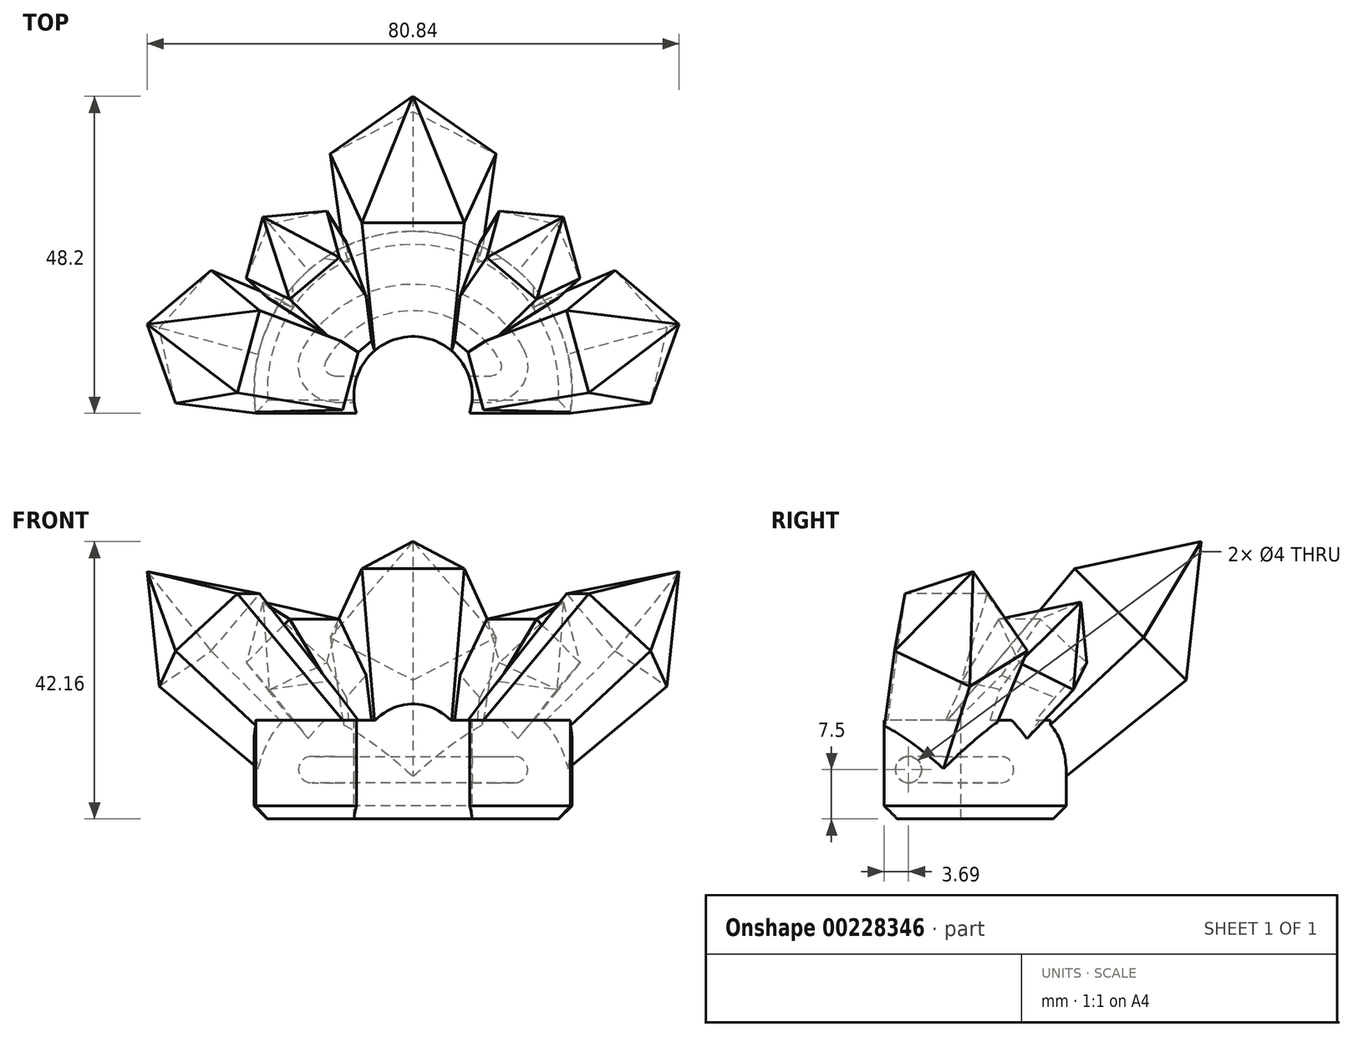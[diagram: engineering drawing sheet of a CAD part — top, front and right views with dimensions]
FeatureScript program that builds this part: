
annotation { "Feature Type Name" : "Feature", "Feature Type Description" : "" }
export const myFeature = defineFeature(function(context is Context, id is Id, definition is map)
    precondition{}
    {
        {
            var Q0;
            Q0=qCreatedBy(makeId("Top.planeOp"),FACE);
            var sketch = newSketch(context, id + "F0", { "sketchPlane" : qUnion([Q0])});
            skLineSegment(sketch, "E0", {"start": v(0, 0) * mm, "end": v(17, 0) * mm, "construction": true});
            skLineSegment(sketch, "E1", {"start": v(0, 0) * mm, "end": v(-17, 0) * mm, "construction": true});
            skArc(sketch, "E2", {"start": v(17, 0) * mm, "mid": v(0, 15) * mm, "end": v(-17, 0) * mm, "construction": true});
            skCircle(sketch, "E3.cCircle", {"center": v(0, 15) * mm, "radius": 8.1 * mm, "construction": true});
            skLineSegment(sketch, "E3.0", {"start": v(0, 25) * mm, "end": v(9.51, 18.1) * mm});
            skLineSegment(sketch, "E3.1", {"start": v(9.51, 18.1) * mm, "end": v(5.88, 6.9) * mm});
            skLineSegment(sketch, "E3.2", {"start": v(5.88, 6.9) * mm, "end": v(-5.88, 6.9) * mm});
            skLineSegment(sketch, "E3.3", {"start": v(-5.88, 6.9) * mm, "end": v(-9.51, 18.1) * mm});
            skLineSegment(sketch, "E3.4", {"start": v(-9.51, 18.1) * mm, "end": v(0, 25) * mm});
            skPoint(sketch, "E3.0.midPoint", {"position": v(4.76, 21.55) * mm});
            skLineSegment(sketch, "E4", {"start": v(0, 0) * mm, "end": v(-18.62, 22.2) * mm, "construction": true});
            skLineSegment(sketch, "E5", {"start": v(0, 0) * mm, "end": v(20.56, 24.5) * mm, "construction": true});
            skCircle(sketch, "E6.cCircle", {"center": v(-9.93, 11.83) * mm, "radius": 5.03 * mm, "construction": true});
            skLineSegment(sketch, "E6.0", {"start": v(-13.93, 16.6) * mm, "end": v(-6.63, 17.1) * mm});
            skLineSegment(sketch, "E6.1", {"start": v(-6.63, 17.1) * mm, "end": v(-3.89, 10.33) * mm});
            skLineSegment(sketch, "E6.2", {"start": v(-3.89, 10.33) * mm, "end": v(-9.5, 5.62) * mm});
            skLineSegment(sketch, "E6.3", {"start": v(-9.5, 5.62) * mm, "end": v(-15.7, 9.5) * mm});
            skLineSegment(sketch, "E6.4", {"start": v(-15.7, 9.5) * mm, "end": v(-13.93, 16.6) * mm});
            skPoint(sketch, "E6.0.midPoint", {"position": v(-10.28, 16.85) * mm});
            skCircle(sketch, "E7.cCircle", {"center": v(9.93, 11.83) * mm, "radius": 5.03 * mm, "construction": true});
            skPoint(sketch, "E7.cCircle.perimeterSnap0", {"position": v(10.28, 12.25) * mm});
            skLineSegment(sketch, "E7.0", {"start": v(6.63, 17.1) * mm, "end": v(13.93, 16.6) * mm});
            skLineSegment(sketch, "E7.1", {"start": v(13.93, 16.6) * mm, "end": v(15.7, 9.5) * mm});
            skLineSegment(sketch, "E7.2", {"start": v(15.7, 9.5) * mm, "end": v(9.5, 5.62) * mm});
            skLineSegment(sketch, "E7.3", {"start": v(9.5, 5.62) * mm, "end": v(3.89, 10.33) * mm});
            skLineSegment(sketch, "E7.4", {"start": v(3.89, 10.33) * mm, "end": v(6.63, 17.1) * mm});
            skPoint(sketch, "E7.0.midPoint", {"position": v(10.28, 16.85) * mm});
            skPoint(sketch, "E7.0.midPoint.positionSnap0", {"position": v(10.28, 12.25) * mm});
            skLineSegment(sketch, "E8", {"start": v(0, 0) * mm, "end": v(0, 46.04) * mm, "construction": true});
            skLineSegment(sketch, "E9", {"start": v(0, 0) * mm, "end": v(-35.68, 9.56) * mm, "construction": true});
            skLineSegment(sketch, "E10", {"start": v(0, 0) * mm, "end": v(44.39, 11.9) * mm, "construction": true});
            skPoint(sketch, "E11", {"position": v(-15.9, 4.26) * mm});
            skPoint(sketch, "E12", {"position": v(15.9, 4.26) * mm});
            skCircle(sketch, "E13.cCircle", {"center": v(-15.9, 4.26) * mm, "radius": 6.7 * mm, "construction": true});
            skLineSegment(sketch, "E13.0", {"start": v(-23.9, 6.4) * mm, "end": v(-16.33, 12.53) * mm});
            skLineSegment(sketch, "E13.1", {"start": v(-16.33, 12.53) * mm, "end": v(-8.16, 7.23) * mm});
            skLineSegment(sketch, "E13.2", {"start": v(-8.16, 7.23) * mm, "end": v(-10.68, -2.18) * mm});
            skLineSegment(sketch, "E13.3", {"start": v(-10.68, -2.18) * mm, "end": v(-20.4, -2.69) * mm});
            skLineSegment(sketch, "E13.4", {"start": v(-20.4, -2.69) * mm, "end": v(-23.9, 6.4) * mm});
            skPoint(sketch, "E13.0.midPoint", {"position": v(-20.11, 9.47) * mm});
            skCircle(sketch, "E14.cCircle", {"center": v(15.9, 4.26) * mm, "radius": 6.7 * mm, "construction": true});
            skLineSegment(sketch, "E14.0", {"start": v(16.33, 12.53) * mm, "end": v(23.9, 6.4) * mm});
            skLineSegment(sketch, "E14.1", {"start": v(23.9, 6.4) * mm, "end": v(20.4, -2.69) * mm});
            skLineSegment(sketch, "E14.2", {"start": v(20.4, -2.69) * mm, "end": v(10.68, -2.18) * mm});
            skLineSegment(sketch, "E14.3", {"start": v(10.68, -2.18) * mm, "end": v(8.16, 7.23) * mm});
            skLineSegment(sketch, "E14.4", {"start": v(8.16, 7.23) * mm, "end": v(16.33, 12.53) * mm});
            skPoint(sketch, "E14.0.midPoint", {"position": v(20.11, 9.47) * mm});
            skLineSegment(sketch, "E15", {"start": v(-23.9, -2.69) * mm, "end": v(23.9, -2.69) * mm});
            skLineSegment(sketch, "E16", {"start": v(-23.9, 6.4) * mm, "end": v(-23.9, -12.7) * mm, "construction": true});
            skLineSegment(sketch, "E17", {"start": v(23.9, 6.4) * mm, "end": v(23.9, -14.68) * mm, "construction": true});
            skArc(sketch, "E18", {"start": v(23.9, -2.69) * mm, "mid": v(0, 25) * mm, "end": v(-23.9, -2.69) * mm});
            skLineSegment(sketch, "E19.top", {"start": v(-23.9, -5.6) * mm, "end": v(23.9, -5.6) * mm});
            skLineSegment(sketch, "E19.left", {"start": v(-23.9, -2.69) * mm, "end": v(-23.9, -5.6) * mm});
            skLineSegment(sketch, "E19.right", {"start": v(23.9, -2.69) * mm, "end": v(23.9, -5.6) * mm});
            skSolve(sketch);
        }
        {
            var Q0;
            Q0=qCreatedBy(makeId("Top.planeOp"),FACE);
            var sketch = newSketch(context, id + "F1", { "sketchPlane" : qUnion([Q0])});
            skArc(sketch, "E20.0", {"start": v(18.92, 0.72) * mm, "mid": v(0, 17) * mm, "end": v(-18.92, 0.72) * mm});
            skCircle(sketch, "E21", {"center": v(0, 0) * mm, "radius": 9 * mm});
            skLineSegment(sketch, "E22.0", {"start": v(-17.44, -1) * mm, "end": v(0, -1) * mm});
            skLineSegment(sketch, "E23.trimOffspring", {"start": v(-14.93, 1) * mm, "end": v(14.93, 1) * mm, "construction": true});
            skLineSegment(sketch, "E24.trimOffspring", {"start": v(-11.91, 3) * mm, "end": v(0, 3) * mm});
            skArc(sketch, "E25.trimOffspring", {"start": v(13.22, 5.23) * mm, "mid": v(0, 13) * mm, "end": v(-13.22, 5.23) * mm});
            skArc(sketch, "E26.trimOffspring", {"start": v(16.36, 2.94) * mm, "mid": v(0, 15) * mm, "end": v(-16.36, 2.94) * mm, "construction": true});
            skLineSegment(sketch, "E27", {"start": v(0, 3) * mm, "end": v(0, 1) * mm});
            skLineSegment(sketch, "E28", {"start": v(0, 3) * mm, "end": v(11.91, 3) * mm});
            skLineSegment(sketch, "E29", {"start": v(0, 1) * mm, "end": v(0, -1) * mm});
            skLineSegment(sketch, "E30", {"start": v(0, -1) * mm, "end": v(17.44, -1) * mm});
            skPoint(sketch, "E31.visualSharp", {"position": v(19.1, -1) * mm});
            skArc(sketch, "E31.filletArc", {"start": v(17.44, -1) * mm, "mid": v(18.57, -0.48) * mm, "end": v(18.92, 0.72) * mm});
            skPoint(sketch, "E32.visualSharp", {"position": v(-19.1, -1) * mm});
            skArc(sketch, "E32.filletArc", {"start": v(-18.92, 0.72) * mm, "mid": v(-18.57, -0.48) * mm, "end": v(-17.44, -1) * mm});
            skPoint(sketch, "E33.newPointB", {"position": v(-18.43, 3) * mm});
            skArc(sketch, "E33.filletArc", {"start": v(-13.22, 5.23) * mm, "mid": v(-13.2, 3.74) * mm, "end": v(-11.91, 3) * mm});
            skArc(sketch, "E34.filletArc", {"start": v(11.91, 3) * mm, "mid": v(13.2, 3.74) * mm, "end": v(13.22, 5.23) * mm});
            skPoint(sketch, "E35.visualSharp", {"position": v(16.84, 1) * mm});
            skArc(sketch, "E35.filletArc", {"start": v(14.93, 1) * mm, "mid": v(16.14, 1.61) * mm, "end": v(16.36, 2.94) * mm, "construction": true});
            skPoint(sketch, "E36.visualSharp", {"position": v(-16.84, 1) * mm});
            skArc(sketch, "E36.filletArc", {"start": v(-16.36, 2.94) * mm, "mid": v(-16.14, 1.61) * mm, "end": v(-14.93, 1) * mm, "construction": true});
            skSolve(sketch);
        }
        {
            var Q0;
            Q0=qCreatedBy(makeId("Front.planeOp"),FACE);
            var sketch = newSketch(context, id + "F2", { "sketchPlane" : qUnion([Q0])});
            skCircle(sketch, "E37", {"center": v(-17, -7.5) * mm, "radius": 2 * mm});
            skCircle(sketch, "E38", {"center": v(17, -7.5) * mm, "radius": 2 * mm});
            skSolve(sketch);
        }
        {
            var Q0;
            {var subQ0=sQuery(id+"F0.wireOp",EDGE,"E13.0");Q0=makeQuery(id+"F0.imprint","IMPRINT",FACE,{"disambiguationData":[TD([[makeQuery(id+"F0.imprint","IMPRINT",EDGE,{"derivedFrom":subQ0}),-1.0]])]});}
            var Q1;
            {var subQ0=sQuery(id+"F0.wireOp",EDGE,"E13.1");var subQ1=sQuery(id+"F0.wireOp",EDGE,"E2");var subQ2=makeQuery(id+"F0.imprint","INTERSECT",VERTEX,{"derivedFrom":[subQ1,subQ0]});Q1=makeQuery(id+"F0.imprint","IMPRINT",FACE,{"disambiguationData":[TD([[makeQuery(id+"F0.imprint","IMPRINT",EDGE,{"disambiguationData":[TD([[subQ2,-1.0]])],"derivedFrom":subQ1}),-1.0]])]});}
            var Q2;
            {var subQ0=sQuery(id+"F0.wireOp",EDGE,"E13.1");var subQ1=sQuery(id+"F0.wireOp",EDGE,"E2");var subQ2=makeQuery(id+"F0.imprint","INTERSECT",VERTEX,{"derivedFrom":[subQ1,subQ0]});Q2=makeQuery(id+"F0.imprint","IMPRINT",FACE,{"disambiguationData":[TD([[makeQuery(id+"F0.imprint","IMPRINT",EDGE,{"disambiguationData":[TD([[subQ2,-1.0]])],"derivedFrom":subQ1}),1.0]])]});}
            var Q3;
            {var subQ0=sQuery(id+"F0.wireOp",EDGE,"E6.3");var subQ6=sQuery(id+"F0.wireOp",EDGE,"E2");var subQ10=makeQuery(id+"F0.imprint","INTERSECT",VERTEX,{"derivedFrom":[subQ6,subQ0]});Q3=makeQuery(id+"F0.imprint","IMPRINT",FACE,{"disambiguationData":[TD([[makeQuery(id+"F0.imprint","IMPRINT",EDGE,{"disambiguationData":[TD([[subQ10,-1.0]])],"derivedFrom":subQ6}),1.0]])]});}
            var Q4;
            {var subQ0=sQuery(id+"F0.wireOp",EDGE,"E2");var subQ1=sQuery(id+"F0.wireOp",EDGE,"E1");var subQ2=makeQuery(id+"F0.imprint","INTERSECT",VERTEX,{"derivedFrom":[subQ1,subQ0]});Q4=makeQuery(id+"F0.imprint","IMPRINT",FACE,{"disambiguationData":[TD([[makeQuery(id+"F0.imprint","IMPRINT",EDGE,{"disambiguationData":[TD([[subQ2,1.0]])],"derivedFrom":subQ1}),-1.0]])]});}
            var Q5;
            {var subQ4=sQuery(id+"F0.wireOp",EDGE,"E13.3");Q5=makeQuery(id+"F0.imprint","IMPRINT",FACE,{"disambiguationData":[TD([[makeQuery(id+"F0.imprint","IMPRINT",EDGE,{"derivedFrom":subQ4}),-1.0]])]});}
            var Q6;
            {var subQ0=sQuery(id+"F0.wireOp",EDGE,"E7.2");var subQ1=sQuery(id+"F0.wireOp",EDGE,"E2");var subQ2=makeQuery(id+"F0.imprint","INTERSECT",VERTEX,{"derivedFrom":[subQ1,subQ0]});Q6=makeQuery(id+"F0.imprint","IMPRINT",FACE,{"disambiguationData":[TD([[makeQuery(id+"F0.imprint","IMPRINT",EDGE,{"disambiguationData":[TD([[subQ2,-1.0]])],"derivedFrom":subQ1}),1.0]])]});}
            var Q7;
            {var subQ0=sQuery(id+"F0.wireOp",EDGE,"E7.2");var subQ1=sQuery(id+"F0.wireOp",EDGE,"E2");var subQ2=makeQuery(id+"F0.imprint","INTERSECT",VERTEX,{"derivedFrom":[subQ1,subQ0]});Q7=makeQuery(id+"F0.imprint","IMPRINT",FACE,{"disambiguationData":[TD([[makeQuery(id+"F0.imprint","IMPRINT",EDGE,{"disambiguationData":[TD([[subQ2,-1.0]])],"derivedFrom":subQ1}),-1.0]])]});}
            var Q8;
            {var subQ0=sQuery(id+"F0.wireOp",EDGE,"E14.0");Q8=makeQuery(id+"F0.imprint","IMPRINT",FACE,{"disambiguationData":[TD([[makeQuery(id+"F0.imprint","IMPRINT",EDGE,{"derivedFrom":subQ0}),-1.0]])]});}
            var Q9;
            {var subQ0=sQuery(id+"F0.wireOp",EDGE,"E14.1");Q9=makeQuery(id+"F0.imprint","IMPRINT",FACE,{"disambiguationData":[TD([[makeQuery(id+"F0.imprint","IMPRINT",EDGE,{"derivedFrom":subQ0}),-1.0]])]});}
            var Q10;
            {var subQ7=sQuery(id+"F0.wireOp",EDGE,"E10");var subQ9=sQuery(id+"F0.wireOp",EDGE,"E2");var subQ11=makeQuery(id+"F0.imprint","INTERSECT",VERTEX,{"derivedFrom":[subQ9,subQ7]});Q10=makeQuery(id+"F0.imprint","IMPRINT",FACE,{"disambiguationData":[TD([[makeQuery(id+"F0.imprint","IMPRINT",EDGE,{"disambiguationData":[TD([[subQ11,-1.0]])],"derivedFrom":subQ9}),1.0]])]});}
            var Q11;
            {var subQ0=sQuery(id+"F0.wireOp",EDGE,"E2");var subQ1=sQuery(id+"F0.wireOp",EDGE,"E0");var subQ2=makeQuery(id+"F0.imprint","INTERSECT",VERTEX,{"derivedFrom":[subQ1,subQ0]});Q11=makeQuery(id+"F0.imprint","IMPRINT",FACE,{"disambiguationData":[TD([[makeQuery(id+"F0.imprint","IMPRINT",EDGE,{"disambiguationData":[TD([[subQ2,1.0]])],"derivedFrom":subQ1}),1.0]])]});}
            var Q12;
            {var subQ0=sQuery(id+"F0.wireOp",EDGE,"E14.2");Q12=makeQuery(id+"F0.imprint","IMPRINT",FACE,{"disambiguationData":[TD([[makeQuery(id+"F0.imprint","IMPRINT",EDGE,{"derivedFrom":subQ0}),-1.0]])]});}
            var Q13;
            {var subQ0=sQuery(id+"F0.wireOp",EDGE,"E10");var subQ1=sQuery(id+"F0.wireOp",EDGE,"E2");var subQ2=makeQuery(id+"F0.imprint","INTERSECT",VERTEX,{"derivedFrom":[subQ1,subQ0]});Q13=makeQuery(id+"F0.imprint","IMPRINT",FACE,{"disambiguationData":[TD([[makeQuery(id+"F0.imprint","IMPRINT",EDGE,{"disambiguationData":[TD([[subQ2,-1.0]])],"derivedFrom":subQ1}),-1.0]])]});}
            var Q14;
            {var subQ1=sQuery(id+"F0.wireOp",EDGE,"E2");var subQ10=sQuery(id+"F0.wireOp",EDGE,"E6.3");var subQ13=makeQuery(id+"F0.imprint","INTERSECT",VERTEX,{"derivedFrom":[subQ1,subQ10]});Q14=makeQuery(id+"F0.imprint","IMPRINT",FACE,{"disambiguationData":[TD([[makeQuery(id+"F0.imprint","IMPRINT",EDGE,{"disambiguationData":[TD([[subQ13,-1.0]])],"derivedFrom":subQ1}),-1.0]])]});}
            var Q15;
            {var subQ0=sQuery(id+"F0.wireOp",EDGE,"E13.4");Q15=makeQuery(id+"F0.imprint","IMPRINT",FACE,{"disambiguationData":[TD([[makeQuery(id+"F0.imprint","IMPRINT",EDGE,{"derivedFrom":subQ0}),-1.0]])]});}
            var Q16;
            {var subQ0=sQuery(id+"F0.wireOp",EDGE,"E6.3");Q16=makeQuery(id+"F0.imprint","IMPRINT",FACE,{"disambiguationData":[TD([[makeQuery(id+"F0.imprint","IMPRINT",EDGE,{"derivedFrom":subQ0}),-1.0]])]});}
            var Q17;
            {var subQ0=sQuery(id+"F0.wireOp",EDGE,"E7.2");Q17=makeQuery(id+"F0.imprint","IMPRINT",FACE,{"disambiguationData":[TD([[makeQuery(id+"F0.imprint","IMPRINT",EDGE,{"derivedFrom":subQ0}),-1.0]])]});}
            extrude(context, id + "F3", {"entities" : qUnion([Q0, Q1, Q2, Q3, Q4, Q5, Q6, Q7, Q8, Q9, Q10, Q11, Q12, Q13, Q14, Q15, Q16, Q17]), "depth" : 25 * mm, "hasDraft" : true, "draftAngle" : 5 * degree});
        }
        {
            var Q0;
            Q0=makeQuery(id+"F3.opExtrude","SWEPT_BODY",BODY,{"disambiguationData":[OSD([sQuery(id+"F0.wireOp",EDGE,"E13.0"),sQuery(id+"F0.wireOp",EDGE,"E13.1"),sQuery(id+"F0.wireOp",EDGE,"E13.2"),sQuery(id+"F0.wireOp",EDGE,"E13.3"),sQuery(id+"F0.wireOp",EDGE,"E13.4")])]});
            var Q1;
            Q1=sQuery(id+"F0.wireOp",EDGE,"E13.2");
            transform(context, id + "F4", {"entities" : qUnion([Q0]), "transformType" : TransformType.ROTATION, "transformAxis" : qUnion([Q1]), "angle" : 45 * degree, "makeCopy" : false});
        }
        {
            var Q0;
            Q0=makeQuery(id+"F3.opExtrude","CAP_FACE",FACE,{"disambiguationData":[OSD([sQuery(id+"F0.wireOp",EDGE,"E13.0"),sQuery(id+"F0.wireOp",EDGE,"E13.1"),sQuery(id+"F0.wireOp",EDGE,"E13.2"),sQuery(id+"F0.wireOp",EDGE,"E13.3"),sQuery(id+"F0.wireOp",EDGE,"E13.4")])],"isStart":false});
            extrude(context, id + "F5", {"entities" : qUnion([Q0]), "operationType" : NewBodyOperationType.ADD, "depth" : 16 * mm, "hasDraft" : true, "draftAngle" : 33 * degree, "draftPullDirection" : true});
        }
        {
            var Q0;
            Q0=makeQuery(id+"F3.opExtrude","SWEPT_BODY",BODY,{"disambiguationData":[OSD([sQuery(id+"F0.wireOp",EDGE,"E14.0"),sQuery(id+"F0.wireOp",EDGE,"E14.1"),sQuery(id+"F0.wireOp",EDGE,"E14.2"),sQuery(id+"F0.wireOp",EDGE,"E14.3"),sQuery(id+"F0.wireOp",EDGE,"E14.4")])]});
            var Q1;
            Q1=sQuery(id+"F0.wireOp",EDGE,"E14.3");
            transform(context, id + "F6", {"entities" : qUnion([Q0]), "transformType" : TransformType.ROTATION, "transformAxis" : qUnion([Q1]), "angle" : 45 * degree, "makeCopy" : false});
        }
        {
            var Q0;
            Q0=makeQuery(id+"F3.opExtrude","CAP_FACE",FACE,{"disambiguationData":[OSD([sQuery(id+"F0.wireOp",EDGE,"E14.0"),sQuery(id+"F0.wireOp",EDGE,"E14.1"),sQuery(id+"F0.wireOp",EDGE,"E14.2"),sQuery(id+"F0.wireOp",EDGE,"E14.3"),sQuery(id+"F0.wireOp",EDGE,"E14.4")])],"isStart":false});
            extrude(context, id + "F7", {"entities" : qUnion([Q0]), "operationType" : NewBodyOperationType.ADD, "depth" : 19 * mm, "hasDraft" : true, "draftAngle" : 33 * degree, "draftPullDirection" : true});
        }
        {
            var Q0;
            {var subQ1=sQuery(id+"F0.wireOp",EDGE,"E3.2");Q0=makeQuery(id+"F0.imprint","IMPRINT",FACE,{"disambiguationData":[TD([[makeQuery(id+"F0.imprint","IMPRINT",EDGE,{"derivedFrom":subQ1}),-1.0]])]});}
            var Q1;
            {var subQ0=sQuery(id+"F0.wireOp",EDGE,"E3.1");var subQ1=sQuery(id+"F0.wireOp",EDGE,"E2");var subQ2=makeQuery(id+"F0.imprint","INTERSECT",VERTEX,{"derivedFrom":[subQ1,subQ0]});Q1=makeQuery(id+"F0.imprint","IMPRINT",FACE,{"disambiguationData":[TD([[makeQuery(id+"F0.imprint","IMPRINT",EDGE,{"disambiguationData":[TD([[subQ2,-1.0]])],"derivedFrom":subQ1}),1.0]])]});}
            var Q2;
            {var subQ1=sQuery(id+"F0.wireOp",EDGE,"E3.0");Q2=makeQuery(id+"F0.imprint","IMPRINT",FACE,{"disambiguationData":[TD([[makeQuery(id+"F0.imprint","IMPRINT",EDGE,{"derivedFrom":subQ1}),-1.0]])]});}
            var Q3;
            {var subQ0=sQuery(id+"F0.wireOp",EDGE,"E3.1");var subQ1=sQuery(id+"F0.wireOp",EDGE,"E2");var subQ2=makeQuery(id+"F0.imprint","INTERSECT",VERTEX,{"derivedFrom":[subQ1,subQ0]});Q3=makeQuery(id+"F0.imprint","IMPRINT",FACE,{"disambiguationData":[TD([[makeQuery(id+"F0.imprint","IMPRINT",EDGE,{"disambiguationData":[TD([[subQ2,-1.0]])],"derivedFrom":subQ1}),-1.0]])]});}
            var Q4;
            {var subQ0=sQuery(id+"F0.wireOp",EDGE,"E6.1");var subQ1=sQuery(id+"F0.wireOp",EDGE,"E2");var subQ2=makeQuery(id+"F0.imprint","INTERSECT",VERTEX,{"derivedFrom":[subQ1,subQ0]});Q4=makeQuery(id+"F0.imprint","IMPRINT",FACE,{"disambiguationData":[TD([[makeQuery(id+"F0.imprint","IMPRINT",EDGE,{"disambiguationData":[TD([[subQ2,-1.0]])],"derivedFrom":subQ1}),1.0]])]});}
            var Q5;
            {var subQ0=sQuery(id+"F0.wireOp",EDGE,"E6.1");var subQ1=sQuery(id+"F0.wireOp",EDGE,"E2");var subQ2=makeQuery(id+"F0.imprint","INTERSECT",VERTEX,{"derivedFrom":[subQ1,subQ0]});Q5=makeQuery(id+"F0.imprint","IMPRINT",FACE,{"disambiguationData":[TD([[makeQuery(id+"F0.imprint","IMPRINT",EDGE,{"disambiguationData":[TD([[subQ2,-1.0]])],"derivedFrom":subQ1}),-1.0]])]});}
            var Q6;
            {var subQ5=sQuery(id+"F0.wireOp",EDGE,"E6.1");Q6=makeQuery(id+"F0.imprint","IMPRINT",FACE,{"disambiguationData":[TD([[makeQuery(id+"F0.imprint","IMPRINT",EDGE,{"derivedFrom":subQ5}),-1.0]])]});}
            var Q7;
            {var subQ5=sQuery(id+"F0.wireOp",EDGE,"E7.4");Q7=makeQuery(id+"F0.imprint","IMPRINT",FACE,{"disambiguationData":[TD([[makeQuery(id+"F0.imprint","IMPRINT",EDGE,{"derivedFrom":subQ5}),-1.0]])]});}
            extrude(context, id + "F8", {"entities" : qUnion([Q0, Q1, Q2, Q3, Q4, Q5, Q6, Q7]), "depth" : 30 * mm, "hasDraft" : true, "draftAngle" : 5 * degree});
        }
        {
            var Q0;
            Q0=makeQuery(id+"F8.opExtrude","CAP_EDGE",EDGE,{"disambiguationData":[OSD([sQuery(id+"F0.wireOp",EDGE,"E3.2")])],"isStart":true});
            cPoint(context, id + "F9", {"entities" : qUnion([Q0]), "parameter" : 0.5});
        }
        {
            var Q0;
            Q0=makeQuery(id+"F8.opExtrude","SWEPT_BODY",BODY,{"disambiguationData":[OSD([sQuery(id+"F0.wireOp",EDGE,"E3.0"),sQuery(id+"F0.wireOp",EDGE,"E3.1"),sQuery(id+"F0.wireOp",EDGE,"E3.2"),sQuery(id+"F0.wireOp",EDGE,"E3.3"),sQuery(id+"F0.wireOp",EDGE,"E3.4")])]});
            var Q1;
            Q1 = qCreatedBy(id + "F9" ,VERTEX);
            var Q2;
            Q2=makeQuery(id+"F8.opExtrude","CAP_EDGE",EDGE,{"disambiguationData":[OSD([sQuery(id+"F0.wireOp",EDGE,"E3.2")])],"isStart":true});
            transform(context, id + "F10", {"entities" : qUnion([Q0]), "transformType" : TransformType.ROTATION, "transformAxis" : qUnion([Q2]), "angle" : 45 * degree, "makeCopy" : false});
        }
        {
            var Q0;
            Q0=makeQuery(id+"F8.opExtrude","CAP_FACE",FACE,{"disambiguationData":[OSD([sQuery(id+"F0.wireOp",EDGE,"E3.0"),sQuery(id+"F0.wireOp",EDGE,"E3.1"),sQuery(id+"F0.wireOp",EDGE,"E3.2"),sQuery(id+"F0.wireOp",EDGE,"E3.3"),sQuery(id+"F0.wireOp",EDGE,"E3.4")])],"isStart":false});
            extrude(context, id + "F11", {"entities" : qUnion([Q0]), "operationType" : NewBodyOperationType.ADD, "depth" : 18 * mm, "hasDraft" : true, "draftAngle" : 33 * degree, "draftPullDirection" : true});
        }
        {
            var Q0;
            {var subQ1=sQuery(id+"F0.wireOp",EDGE,"E3.1");var subQ6=sQuery(id+"F0.wireOp",EDGE,"E7.0");var subQ9=makeQuery(id+"F0.imprint","INTERSECT",VERTEX,{"derivedFrom":[subQ1,subQ6]});Q0=makeQuery(id+"F0.imprint","IMPRINT",FACE,{"disambiguationData":[TD([[makeQuery(id+"F0.imprint","IMPRINT",EDGE,{"disambiguationData":[TD([[subQ9,-1.0]])],"derivedFrom":subQ1}),1.0]])]});}
            var Q1;
            {var subQ0=sQuery(id+"F0.wireOp",EDGE,"E7.2");Q1=makeQuery(id+"F0.imprint","IMPRINT",FACE,{"disambiguationData":[TD([[makeQuery(id+"F0.imprint","IMPRINT",EDGE,{"derivedFrom":subQ0}),-1.0]])]});}
            var Q2;
            {var subQ5=sQuery(id+"F0.wireOp",EDGE,"E7.4");Q2=makeQuery(id+"F0.imprint","IMPRINT",FACE,{"disambiguationData":[TD([[makeQuery(id+"F0.imprint","IMPRINT",EDGE,{"derivedFrom":subQ5}),-1.0]])]});}
            var Q3;
            {var subQ5=sQuery(id+"F0.wireOp",EDGE,"E6.1");Q3=makeQuery(id+"F0.imprint","IMPRINT",FACE,{"disambiguationData":[TD([[makeQuery(id+"F0.imprint","IMPRINT",EDGE,{"derivedFrom":subQ5}),-1.0]])]});}
            var Q4;
            {var subQ5=sQuery(id+"F0.wireOp",EDGE,"E6.2");var subQ6=sQuery(id+"F0.wireOp",EDGE,"E3.3");var subQ7=makeQuery(id+"F0.imprint","INTERSECT",VERTEX,{"derivedFrom":[subQ6,subQ5]});Q4=makeQuery(id+"F0.imprint","IMPRINT",FACE,{"disambiguationData":[TD([[makeQuery(id+"F0.imprint","IMPRINT",EDGE,{"disambiguationData":[TD([[subQ7,-1.0]])],"derivedFrom":subQ6}),1.0]])]});}
            var Q5;
            {var subQ0=sQuery(id+"F0.wireOp",EDGE,"E6.3");Q5=makeQuery(id+"F0.imprint","IMPRINT",FACE,{"disambiguationData":[TD([[makeQuery(id+"F0.imprint","IMPRINT",EDGE,{"derivedFrom":subQ0}),-1.0]])]});}
            extrude(context, id + "F12", {"entities" : qUnion([Q0, Q1, Q2, Q3, Q4, Q5]), "depth" : 20 * mm, "hasDraft" : true, "draftAngle" : 5 * degree});
        }
        {
            var Q0;
            Q0=makeQuery(id+"F12.opExtrude","SWEPT_BODY",BODY,{"disambiguationData":[OSD([sQuery(id+"F0.wireOp",EDGE,"E7.0"),sQuery(id+"F0.wireOp",EDGE,"E7.1"),sQuery(id+"F0.wireOp",EDGE,"E7.2"),sQuery(id+"F0.wireOp",EDGE,"E7.3"),sQuery(id+"F0.wireOp",EDGE,"E7.4")])]});
            var Q1;
            Q1=makeQuery(id+"F12.opExtrude","CAP_EDGE",EDGE,{"disambiguationData":[OSD([sQuery(id+"F0.wireOp",EDGE,"E7.3")])],"isStart":true});
            transform(context, id + "F13", {"entities" : qUnion([Q0]), "transformType" : TransformType.ROTATION, "transformAxis" : qUnion([Q1]), "angle" : 45 * degree, "makeCopy" : false});
        }
        {
            var Q0;
            Q0=makeQuery(id+"F12.opExtrude","CAP_FACE",FACE,{"disambiguationData":[OSD([sQuery(id+"F0.wireOp",EDGE,"E7.0"),sQuery(id+"F0.wireOp",EDGE,"E7.1"),sQuery(id+"F0.wireOp",EDGE,"E7.2"),sQuery(id+"F0.wireOp",EDGE,"E7.3"),sQuery(id+"F0.wireOp",EDGE,"E7.4")])],"isStart":false});
            extrude(context, id + "F14", {"entities" : qUnion([Q0]), "operationType" : NewBodyOperationType.ADD, "depth" : 12 * mm, "hasDraft" : true, "draftAngle" : 33 * degree, "draftPullDirection" : true});
        }
        {
            var Q0;
            Q0=makeQuery(id+"F12.opExtrude","SWEPT_BODY",BODY,{"disambiguationData":[OSD([sQuery(id+"F0.wireOp",EDGE,"E6.0"),sQuery(id+"F0.wireOp",EDGE,"E6.1"),sQuery(id+"F0.wireOp",EDGE,"E6.2"),sQuery(id+"F0.wireOp",EDGE,"E6.3"),sQuery(id+"F0.wireOp",EDGE,"E6.4")])]});
            var Q1;
            Q1=makeQuery(id+"F12.opExtrude","CAP_EDGE",EDGE,{"disambiguationData":[OSD([sQuery(id+"F0.wireOp",EDGE,"E6.2")])],"isStart":true});
            transform(context, id + "F15", {"entities" : qUnion([Q0]), "transformType" : TransformType.ROTATION, "transformAxis" : qUnion([Q1]), "angle" : 45 * degree, "makeCopy" : false});
        }
        {
            var Q0;
            Q0=makeQuery(id+"F12.opExtrude","CAP_FACE",FACE,{"disambiguationData":[OSD([sQuery(id+"F0.wireOp",EDGE,"E6.0"),sQuery(id+"F0.wireOp",EDGE,"E6.1"),sQuery(id+"F0.wireOp",EDGE,"E6.2"),sQuery(id+"F0.wireOp",EDGE,"E6.3"),sQuery(id+"F0.wireOp",EDGE,"E6.4")])],"isStart":false});
            extrude(context, id + "F16", {"entities" : qUnion([Q0]), "operationType" : NewBodyOperationType.ADD, "depth" : 13 * mm, "hasDraft" : true, "draftAngle" : 33 * degree, "draftPullDirection" : true});
        }
        {
            var Q0;
            {var subQ9=sQuery(id+"F0.wireOp",EDGE,"E3.4");Q0=makeQuery(id+"F0.imprint","IMPRINT",FACE,{"disambiguationData":[TD([[makeQuery(id+"F0.imprint","IMPRINT",EDGE,{"derivedFrom":subQ9}),1.0]])]});}
            var Q1;
            {var subQ1=sQuery(id+"F0.wireOp",EDGE,"E6.3");Q1=makeQuery(id+"F0.imprint","IMPRINT",FACE,{"disambiguationData":[TD([[makeQuery(id+"F0.imprint","IMPRINT",EDGE,{"derivedFrom":subQ1}),1.0]])]});}
            var Q2;
            {var subQ0=sQuery(id+"F0.wireOp",EDGE,"E15");var subQ3=sQuery(id+"F0.wireOp",EDGE,"E18");var subQ5=makeQuery(id+"F0.imprint","INTERSECT",VERTEX,{"disambiguationData":[OD(0.0)],"derivedFrom":[subQ0,subQ3]});Q2=makeQuery(id+"F0.imprint","IMPRINT",FACE,{"disambiguationData":[TD([[makeQuery(id+"F0.imprint","IMPRINT",EDGE,{"disambiguationData":[TD([[subQ5,1.0]])],"derivedFrom":subQ3}),1.0]])]});}
            var Q3;
            {var subQ5=sQuery(id+"F0.wireOp",EDGE,"E6.2");var subQ6=sQuery(id+"F0.wireOp",EDGE,"E3.3");var subQ7=makeQuery(id+"F0.imprint","INTERSECT",VERTEX,{"derivedFrom":[subQ6,subQ5]});Q3=makeQuery(id+"F0.imprint","IMPRINT",FACE,{"disambiguationData":[TD([[makeQuery(id+"F0.imprint","IMPRINT",EDGE,{"disambiguationData":[TD([[subQ7,-1.0]])],"derivedFrom":subQ6}),1.0]])]});}
            var Q4;
            {var subQ0=sQuery(id+"F0.wireOp",EDGE,"E6.3");Q4=makeQuery(id+"F0.imprint","IMPRINT",FACE,{"disambiguationData":[TD([[makeQuery(id+"F0.imprint","IMPRINT",EDGE,{"derivedFrom":subQ0}),-1.0]])]});}
            var Q5;
            {var subQ5=sQuery(id+"F0.wireOp",EDGE,"E6.1");Q5=makeQuery(id+"F0.imprint","IMPRINT",FACE,{"disambiguationData":[TD([[makeQuery(id+"F0.imprint","IMPRINT",EDGE,{"derivedFrom":subQ5}),-1.0]])]});}
            var Q6;
            {var subQ5=sQuery(id+"F0.wireOp",EDGE,"E3.0");Q6=makeQuery(id+"F0.imprint","IMPRINT",FACE,{"disambiguationData":[TD([[makeQuery(id+"F0.imprint","IMPRINT",EDGE,{"derivedFrom":subQ5}),1.0]])]});}
            var Q7;
            {var subQ1=sQuery(id+"F0.wireOp",EDGE,"E3.2");Q7=makeQuery(id+"F0.imprint","IMPRINT",FACE,{"disambiguationData":[TD([[makeQuery(id+"F0.imprint","IMPRINT",EDGE,{"derivedFrom":subQ1}),1.0]])]});}
            var Q8;
            {var subQ9=sQuery(id+"F0.wireOp",EDGE,"E3.0");Q8=makeQuery(id+"F0.imprint","IMPRINT",FACE,{"disambiguationData":[TD([[makeQuery(id+"F0.imprint","IMPRINT",EDGE,{"derivedFrom":subQ9}),-1.0]])]});}
            var Q9;
            {var subQ1=sQuery(id+"F0.wireOp",EDGE,"E3.1");var subQ6=sQuery(id+"F0.wireOp",EDGE,"E7.0");var subQ9=makeQuery(id+"F0.imprint","INTERSECT",VERTEX,{"derivedFrom":[subQ1,subQ6]});Q9=makeQuery(id+"F0.imprint","IMPRINT",FACE,{"disambiguationData":[TD([[makeQuery(id+"F0.imprint","IMPRINT",EDGE,{"disambiguationData":[TD([[subQ9,-1.0]])],"derivedFrom":subQ1}),1.0]])]});}
            var Q10;
            {var subQ5=sQuery(id+"F0.wireOp",EDGE,"E7.4");Q10=makeQuery(id+"F0.imprint","IMPRINT",FACE,{"disambiguationData":[TD([[makeQuery(id+"F0.imprint","IMPRINT",EDGE,{"derivedFrom":subQ5}),-1.0]])]});}
            var Q11;
            {var subQ0=sQuery(id+"F0.wireOp",EDGE,"E7.2");Q11=makeQuery(id+"F0.imprint","IMPRINT",FACE,{"disambiguationData":[TD([[makeQuery(id+"F0.imprint","IMPRINT",EDGE,{"derivedFrom":subQ0}),-1.0]])]});}
            var Q12;
            {var subQ1=sQuery(id+"F0.wireOp",EDGE,"E7.2");Q12=makeQuery(id+"F0.imprint","IMPRINT",FACE,{"disambiguationData":[TD([[makeQuery(id+"F0.imprint","IMPRINT",EDGE,{"derivedFrom":subQ1}),1.0]])]});}
            var Q13;
            {var subQ0=sQuery(id+"F0.wireOp",EDGE,"E15");var subQ3=sQuery(id+"F0.wireOp",EDGE,"E18");var subQ5=makeQuery(id+"F0.imprint","INTERSECT",VERTEX,{"disambiguationData":[OD(1.0)],"derivedFrom":[subQ0,subQ3]});Q13=makeQuery(id+"F0.imprint","IMPRINT",FACE,{"disambiguationData":[TD([[makeQuery(id+"F0.imprint","IMPRINT",EDGE,{"disambiguationData":[TD([[subQ5,-1.0]])],"derivedFrom":subQ3}),1.0]])]});}
            extrude(context, id + "F17", {"entities" : qUnion([Q0, Q1, Q2, Q3, Q4, Q5, Q6, Q7, Q8, Q9, Q10, Q11, Q12, Q13]), "operationType" : NewBodyOperationType.ADD, "oppositeDirection" : true, "depth" : 15 * mm});
        }
        {
            var Q0;
            Q0=makeQuery(id+"F17.opExtrude","CAP_FACE",FACE,{"disambiguationData":[OSD([sQuery(id+"F0.wireOp",EDGE,"E15"),sQuery(id+"F0.wireOp",EDGE,"E18")])],"isStart":false});
            chamfer(context, id + "F18", {"entities" : qUnion([Q0]), "width" : 2 * mm, "tangentPropagation" : true});
        }
        {
            var Q0;
            Q0=makeQuery(id+"F0.imprint","IMPRINT",FACE,{"disambiguationData":[TD([[makeQuery(id+"F0.imprint","IMPRINT",EDGE,{"derivedFrom":sQuery(id+"F0.wireOp",EDGE,"E19.top")}),1.0]])]});
            extrude(context, id + "F19", {"entities" : qUnion([Q0]), "operationType" : NewBodyOperationType.REMOVE, "endBound" : BoundingType.THROUGH_ALL, "oppositeDirection" : true, "depth" : 25 * mm});
        }
        {
            var Q0;
            {var subQ0=sQuery(id+"F1.wireOp",EDGE,"E28");var subQ1=sQuery(id+"F1.wireOp",EDGE,"E21");var subQ2=makeQuery(id+"F1.imprint","INTERSECT",VERTEX,{"derivedFrom":[subQ1,subQ0]});Q0=makeQuery(id+"F1.imprint","IMPRINT",FACE,{"disambiguationData":[TD([[makeQuery(id+"F1.imprint","IMPRINT",EDGE,{"disambiguationData":[TD([[subQ2,-1.0]])],"derivedFrom":subQ1}),1.0]])]});}
            var Q1;
            {var subQ0=sQuery(id+"F1.wireOp",EDGE,"E22.0");var subQ1=sQuery(id+"F1.wireOp",EDGE,"E21");var subQ2=makeQuery(id+"F1.imprint","INTERSECT",VERTEX,{"derivedFrom":[subQ1,subQ0]});Q1=makeQuery(id+"F1.imprint","IMPRINT",FACE,{"disambiguationData":[TD([[makeQuery(id+"F1.imprint","IMPRINT",EDGE,{"disambiguationData":[TD([[subQ2,-1.0]])],"derivedFrom":subQ1}),1.0]])]});}
            var Q2;
            {var subQ5=sQuery(id+"F1.wireOp",EDGE,"E27");Q2=makeQuery(id+"F1.imprint","IMPRINT",FACE,{"disambiguationData":[TD([[makeQuery(id+"F1.imprint","IMPRINT",EDGE,{"derivedFrom":subQ5}),-1.0]])]});}
            var Q3;
            {var subQ5=sQuery(id+"F1.wireOp",EDGE,"E29");Q3=makeQuery(id+"F1.imprint","IMPRINT",FACE,{"disambiguationData":[TD([[makeQuery(id+"F1.imprint","IMPRINT",EDGE,{"derivedFrom":subQ5}),-1.0]])]});}
            var Q4;
            {var subQ5=sQuery(id+"F1.wireOp",EDGE,"E29");Q4=makeQuery(id+"F1.imprint","IMPRINT",FACE,{"disambiguationData":[TD([[makeQuery(id+"F1.imprint","IMPRINT",EDGE,{"derivedFrom":subQ5}),1.0]])]});}
            var Q5;
            {var subQ5=sQuery(id+"F1.wireOp",EDGE,"E27");Q5=makeQuery(id+"F1.imprint","IMPRINT",FACE,{"disambiguationData":[TD([[makeQuery(id+"F1.imprint","IMPRINT",EDGE,{"derivedFrom":subQ5}),1.0]])]});}
            extrude(context, id + "F20", {"entities" : qUnion([Q0, Q1, Q2, Q3, Q4, Q5]), "operationType" : NewBodyOperationType.REMOVE, "oppositeDirection" : true, "depth" : 25 * mm, "hasSecondDirection" : true, "secondDirectionOppositeDirection" : false, "secondDirectionDepth" : 25 * mm});
        }
        {
            var Q0;
            Q0=qCreatedBy(makeId("Right.planeOp"),FACE);
            var sketch = newSketch(context, id + "F21", { "sketchPlane" : qUnion([Q0])});
            skLineSegment(sketch, "E39", {"start": v(0, 0) * mm, "end": v(1, 0) * mm, "construction": true});
            skLineSegment(sketch, "E40", {"start": v(1, 0) * mm, "end": v(1, -7.5) * mm, "construction": true});
            skCircle(sketch, "E41", {"center": v(1, -7.5) * mm, "radius": 2 * mm});
            skSolve(sketch);
        }
        {
            var Q0;
            Q0=makeQuery(id+"F21.imprint","IMPRINT",FACE,{"disambiguationData":[TD([[makeQuery(id+"F21.imprint","IMPRINT",EDGE,{"derivedFrom":sQuery(id+"F21.wireOp",EDGE,"E41")}),1.0]])]});
            var Q1;
            Q1=sQuery(id+"F2.wireOp",EDGE,"E37");
            var Q2;
            Q2=sQuery(id+"F2.wireOp",EDGE,"E38");
            var Q3;
            Q3=sQuery(id+"F1.wireOp",EDGE,"E25.trimOffspring");
            var Q4;
            Q4=sQuery(id+"F1.wireOp",EDGE,"E33.filletArc");
            var Q5;
            Q5=sQuery(id+"F1.wireOp",EDGE,"E24.trimOffspring");
            var Q6;
            Q6=sQuery(id+"F1.wireOp",EDGE,"E28");
            var Q7;
            Q7=sQuery(id+"F1.wireOp",EDGE,"E34.filletArc");
            sweep(context, id + "F22", {"operationType" : NewBodyOperationType.REMOVE, "profiles" : qUnion([Q0]), "surfaceProfiles" : qUnion([Q1, Q2]), "path" : qUnion([Q3, Q4, Q5, Q6, Q7])});
        }
    });
